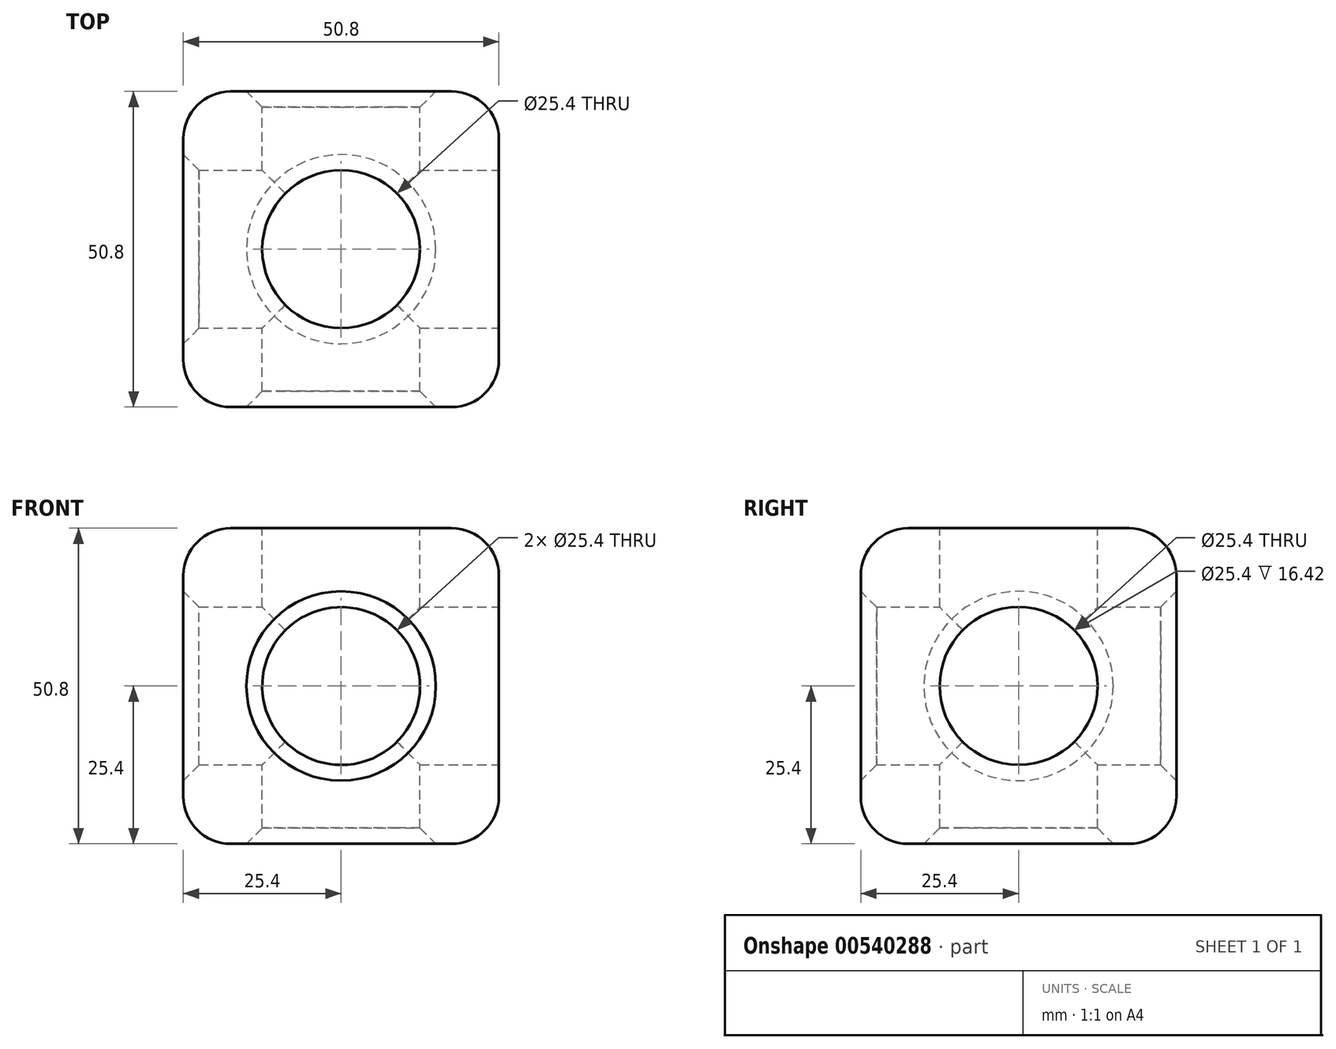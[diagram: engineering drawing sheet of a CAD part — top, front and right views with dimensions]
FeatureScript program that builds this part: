
annotation { "Feature Type Name" : "Feature", "Feature Type Description" : "" }
export const myFeature = defineFeature(function(context is Context, id is Id, definition is map)
    precondition{}
    {
        {
            var Q0;
            Q0=qCreatedBy(makeId("Front.planeOp"),FACE);
            var sketch = newSketch(context, id + "F0", { "sketchPlane" : qUnion([Q0])});
            skLineSegment(sketch, "E0.bottom", {"start": v(0, 0) * mm, "end": v(-50.8, 0) * mm});
            skLineSegment(sketch, "E0.top", {"start": v(0, -50.8) * mm, "end": v(-50.8, -50.8) * mm});
            skLineSegment(sketch, "E0.left", {"start": v(0, 0) * mm, "end": v(0, -50.8) * mm});
            skLineSegment(sketch, "E0.right", {"start": v(-50.8, 0) * mm, "end": v(-50.8, -50.8) * mm});
            skCircle(sketch, "E1", {"center": v(-25.4, -25.4) * mm, "radius": 12.7 * mm});
            skLineSegment(sketch, "E2", {"start": v(-50.8, -25.4) * mm, "end": v(-25.4, -25.4) * mm});
            skSolve(sketch);
        }
        {
            var Q0;
            Q0=makeQuery(id+"F0.imprint","IMPRINT",FACE,{"disambiguationData":[TD([[makeQuery(id+"F0.imprint","IMPRINT",EDGE,{"derivedFrom":sQuery(id+"F0.wireOp",EDGE,"E0.bottom")}),1.0]])]});
            extrude(context, id + "F1", {"entities" : qUnion([Q0]), "depth" : 50.8 * mm, "offsetDistance" : 25.4 * mm});
        }
        {
            var Q0;
            Q0 = qSketchRegion(id + "F0", true);
            extrude(context, id + "F2", {"entities" : qUnion([Q0]), "operationType" : NewBodyOperationType.ADD, "depth" : 50.8 * mm, "offsetDistance" : 25.4 * mm});
        }
        {
            var Q0;
            Q0=makeQuery(id+"F1.opExtrude","SWEPT_FACE",FACE,{"disambiguationData":[OSD([sQuery(id+"F0.wireOp",EDGE,"E0.bottom")])]});
            var sketch = newSketch(context, id + "F3", { "sketchPlane" : qUnion([Q0])});
            skLineSegment(sketch, "E3", {"start": v(-50.8, -25.4) * mm, "end": v(-25.4, -25.4) * mm});
            skCircle(sketch, "E4", {"center": v(-25.4, -25.4) * mm, "radius": 12.7 * mm});
            skSolve(sketch);
        }
        {
            var Q0;
            Q0 = qSketchRegion(id + "F3", true);
            extrude(context, id + "F4", {"entities" : qUnion([Q0]), "operationType" : NewBodyOperationType.REMOVE, "oppositeDirection" : true, "depth" : 80.77 * mm, "offsetDistance" : 25.4 * mm});
        }
        {
            var Q0;
            Q0=makeQuery(id+"F1.opExtrude","SWEPT_FACE",FACE,{"disambiguationData":[OSD([sQuery(id+"F0.wireOp",EDGE,"E0.left")])]});
            var sketch = newSketch(context, id + "F5", { "sketchPlane" : qUnion([Q0])});
            skLineSegment(sketch, "E5", {"start": v(-25.4, 0) * mm, "end": v(-25.4, -25.4) * mm});
            skPoint(sketch, "E5.endSnap0", {"position": v(-25.4, 0) * mm});
            skCircle(sketch, "E6", {"center": v(-25.4, -25.4) * mm, "radius": 12.7 * mm});
            skSolve(sketch);
        }
        {
            var Q0;
            Q0 = qSketchRegion(id + "F5", true);
            extrude(context, id + "F6", {"entities" : qUnion([Q0]), "operationType" : NewBodyOperationType.REMOVE, "oppositeDirection" : true, "depth" : 101.35 * mm, "offsetDistance" : 25.4 * mm});
        }
        {
            var Q0;
            Q0=makeQuery(id+"F1.opExtrude","CAP_EDGE",EDGE,{"disambiguationData":[OSD([sQuery(id+"F0.wireOp",EDGE,"E0.bottom")])],"isStart":false});
            var Q1;
            Q1=makeQuery(id+"F1.opExtrude","SWEPT_EDGE",EDGE,{"disambiguationData":[OSD([sQuery(id+"F0.wireOp",EDGE,"E0.bottom"),sQuery(id+"F0.wireOp",EDGE,"E0.right")])]});
            var Q2;
            Q2=makeQuery(id+"F1.opExtrude","CAP_EDGE",EDGE,{"disambiguationData":[OSD([sQuery(id+"F0.wireOp",EDGE,"E0.bottom")])],"isStart":true});
            var Q3;
            Q3=makeQuery(id+"F1.opExtrude","SWEPT_EDGE",EDGE,{"disambiguationData":[OSD([sQuery(id+"F0.wireOp",EDGE,"E0.bottom"),sQuery(id+"F0.wireOp",EDGE,"E0.left")])]});
            var Q4;
            Q4=makeQuery(id+"F1.opExtrude","CAP_EDGE",EDGE,{"disambiguationData":[OSD([sQuery(id+"F0.wireOp",EDGE,"E0.left")])],"isStart":false});
            var Q5;
            Q5=makeQuery(id+"F1.opExtrude","CAP_EDGE",EDGE,{"disambiguationData":[OSD([sQuery(id+"F0.wireOp",EDGE,"E0.top")])],"isStart":false});
            var Q6;
            Q6=makeQuery(id+"F1.opExtrude","SWEPT_EDGE",EDGE,{"disambiguationData":[OSD([sQuery(id+"F0.wireOp",EDGE,"E0.top"),sQuery(id+"F0.wireOp",EDGE,"E0.left")])]});
            var Q7;
            Q7=makeQuery(id+"F1.opExtrude","CAP_EDGE",EDGE,{"disambiguationData":[OSD([sQuery(id+"F0.wireOp",EDGE,"E0.left")])],"isStart":true});
            var Q8;
            Q8=makeQuery(id+"F1.opExtrude","CAP_EDGE",EDGE,{"disambiguationData":[OSD([sQuery(id+"F0.wireOp",EDGE,"E0.right")])],"isStart":false});
            var Q9;
            Q9=makeQuery(id+"F1.opExtrude","SWEPT_EDGE",EDGE,{"disambiguationData":[OSD([sQuery(id+"F0.wireOp",EDGE,"E0.top"),sQuery(id+"F0.wireOp",EDGE,"E0.right")])]});
            var Q10;
            Q10=makeQuery(id+"F1.opExtrude","CAP_EDGE",EDGE,{"disambiguationData":[OSD([sQuery(id+"F0.wireOp",EDGE,"E0.top")])],"isStart":true});
            var Q11;
            Q11=makeQuery(id+"F1.opExtrude","CAP_EDGE",EDGE,{"disambiguationData":[OSD([sQuery(id+"F0.wireOp",EDGE,"E0.right")])],"isStart":true});
            fillet(context, id + "F7", {"entities" : qUnion([Q0, Q1, Q2, Q3, Q4, Q5, Q6, Q7, Q8, Q9, Q10, Q11]), "radius" : 7.62 * mm, "tangentPropagation" : true, "allowEdgeOverflow" : false});
        }
        {
            var Q0;
            Q0=makeQuery(id+"F4.boolean.opBoolean","COPY",EDGE,{"derivedFrom":makeQuery(id+"F4.opExtrude","CAP_EDGE",EDGE,{"disambiguationData":[OSD([sQuery(id+"F3.wireOp",EDGE,"E4")])],"isStart":true})});
            var Q1;
            Q1=makeQuery(id+"F1.opExtrude","CAP_EDGE",EDGE,{"disambiguationData":[OSD([sQuery(id+"F0.wireOp",EDGE,"E1")])],"isStart":false});
            var Q2;
            Q2=makeQuery(id+"F6.boolean.opBoolean","COPY",EDGE,{"derivedFrom":makeQuery(id+"F6.opExtrude","CAP_EDGE",EDGE,{"disambiguationData":[OSD([sQuery(id+"F5.wireOp",EDGE,"E6")])],"isStart":true})});
            var Q3;
            Q3=makeQuery(id+"F1.opExtrude","CAP_EDGE",EDGE,{"disambiguationData":[OSD([sQuery(id+"F0.wireOp",EDGE,"E1")])],"isStart":true});
            var Q4;
            Q4=makeQuery(id+"F6.boolean.opBoolean","INTERSECT",EDGE,{"derivedFrom":[makeQuery(id+"F1.opExtrude","SWEPT_FACE",FACE,{"disambiguationData":[OSD([sQuery(id+"F0.wireOp",EDGE,"E0.right")])]}),makeQuery(id+"F6.opExtrude","SWEPT_FACE",FACE,{"disambiguationData":[OSD([sQuery(id+"F5.wireOp",EDGE,"E6")])]})]});
            var Q5;
            Q5=makeQuery(id+"F4.boolean.opBoolean","INTERSECT",EDGE,{"derivedFrom":[makeQuery(id+"F1.opExtrude","SWEPT_FACE",FACE,{"disambiguationData":[OSD([sQuery(id+"F0.wireOp",EDGE,"E0.top")])]}),makeQuery(id+"F4.opExtrude","SWEPT_FACE",FACE,{"disambiguationData":[OSD([sQuery(id+"F3.wireOp",EDGE,"E4")])]})]});
            chamfer(context, id + "F8", {"entities" : qUnion([Q0, Q1, Q2, Q3, Q4, Q5]), "width" : 2.54 * mm, "tangentPropagation" : true});
        }
    });
